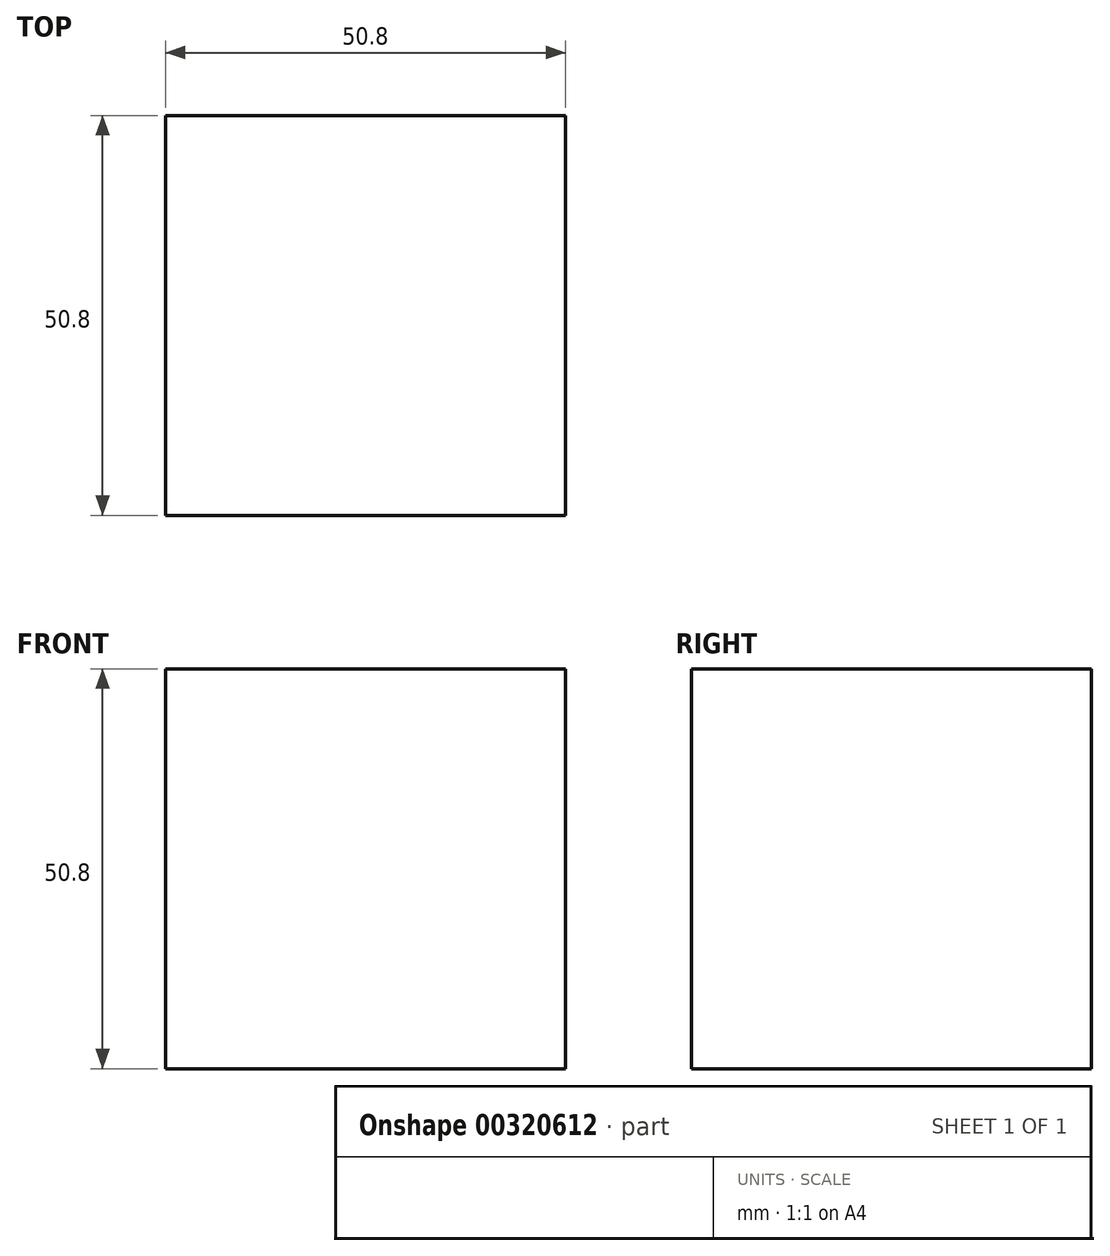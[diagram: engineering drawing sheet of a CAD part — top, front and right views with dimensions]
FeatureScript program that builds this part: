
annotation { "Feature Type Name" : "Feature", "Feature Type Description" : "" }
export const myFeature = defineFeature(function(context is Context, id is Id, definition is map)
    precondition{}
    {
        {
            var Q0;
            Q0=qCreatedBy(makeId("Front.planeOp"),FACE);
            var sketch = newSketch(context, id + "F0", { "sketchPlane" : qUnion([Q0])});
            skLineSegment(sketch, "E0.bottom", {"start": v(-25.4, 25.4) * mm, "end": v(25.4, 25.4) * mm});
            skLineSegment(sketch, "E0.top", {"start": v(-25.4, -25.4) * mm, "end": v(25.4, -25.4) * mm});
            skLineSegment(sketch, "E0.left", {"start": v(-25.4, 25.4) * mm, "end": v(-25.4, -25.4) * mm});
            skLineSegment(sketch, "E0.right", {"start": v(25.4, 25.4) * mm, "end": v(25.4, -25.4) * mm});
            skPoint(sketch, "E0.middle", {"position": v(0, 0) * mm});
            skSolve(sketch);
        }
        {
            var Q0;
            Q0 = qSketchRegion(id + "F0", true);
            extrude(context, id + "F1", {"entities" : qUnion([Q0]), "depth" : 50.8 * mm});
        }
    });
